# Revit family: REDONDO ERC
name_source: partatom
category: Plumbing Fixtures
revit_build: Autodesk Revit 2017 (Build: 20160225_1515(x64)
units: mm (PartAtom-declared; Revit-internal decimal feet)

## family parameters
Cut with Voids When Loaded = Yes
Host = Face
Part Type = Normal
Room Calculation Point = No
Round Connector Dimension = Use Diameter
Shared = No

## types (1)
- Redondo ERC
    Acabado Lavaplato = Teka_Acero Inoxidable
    Ca_1_Accesorios = Válvula 3 1/2'' + Rebalse +Sifón
    Ca_1_Dimensiones Lavaplatos = Φ 450 mm
    Ca_1_Dimesiones Cubeta = Φ 385 mm
    Ca_1_Espesor de acero = 0.8 mm
    Ca_1_Instalación = Empotrado
    Ca_1_Material Principal = Acero Inoxidable AISI-304 (18/10)
    Ca_1_Profundidad Cubeta = 180 mm
    Ca_1_Sello CE = Producto cumple Norma Europea EN-13310
    Ca_Certificaciones = Norma Europea EN-13310
    Ca_Creado por = Catálogo Arquitectura
    Ca_Código Catálogo Arquitectura = 411_TEK_049
    Ca_Código EAN = 8421152031100
    Ca_Código del Producto = 10108010
    Ca_Especificaciones Técnicas = Lavaplatos empotrable de acero TEKA modelo Redondo ERC
    Ca_Fabricante = Teka
    Ca_Instalación = Empotrado
    Ca_Itemizado CDT = E 04 05 01
    Ca_Masterformat = 22 41 16
    Ca_Material Principal = Acero Inoxidable AISI-304 (18/10)
    Ca_País de Fabricación = España
    Ca_Producto = Lavaplatos Redondo ERC
    Ca_Profundidad = 180 mm  [stored 0.590551 ft]
    Ca_Representante = Teka
    Ca_Teléfono = 99821 1017
    Ca_Usos = Lavaplatos empotrable para cocina
    Ca_Web del Fabricante = www.teka.cl
    Ca_Web del Representante = www.teka.cl
    Default Elevation = 1219.2 mm  [stored 4 ft]
    Description = Lavaplatos empotrable para cocina
    Diametro Exterior = 450 mm  [stored 1.47638 ft]
    Diametro Interior = 385 mm  [stored 1.26312 ft]
    Manufacturer = Teka
    Model = Redondo ERC
    URL = www.teka.cl
    Waste Connection = Yes

note: [stored X ft] marks values corroborated as IEEE doubles in the binary element streams (Revit-internal decimal feet)
